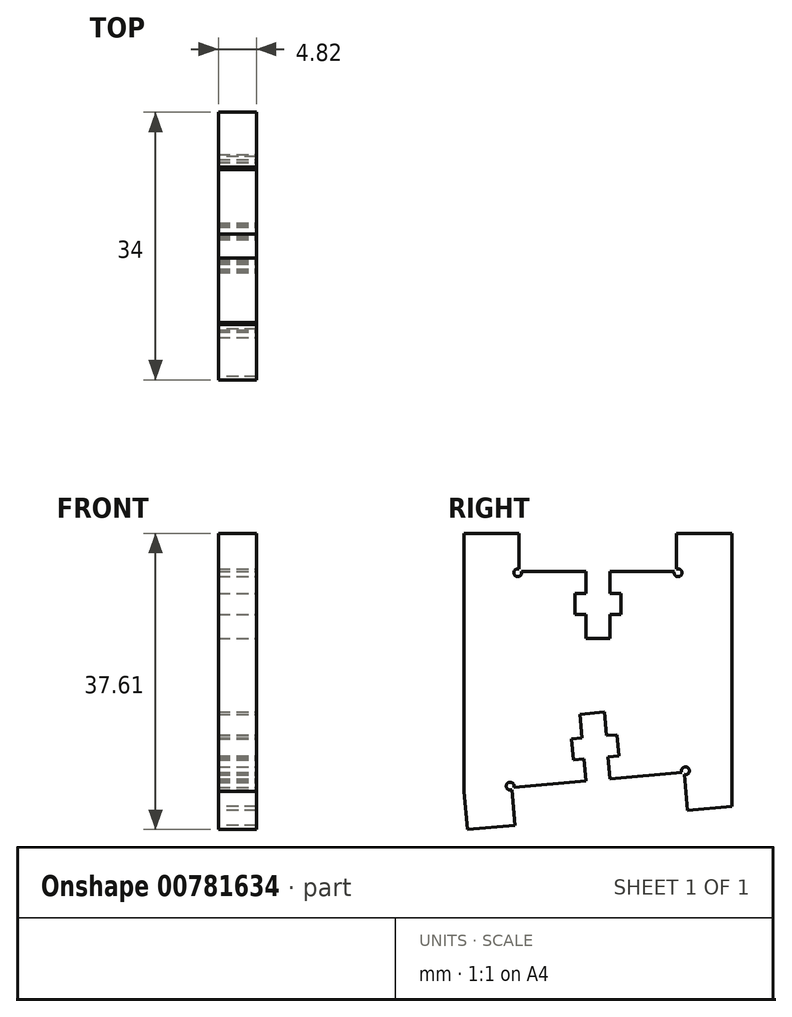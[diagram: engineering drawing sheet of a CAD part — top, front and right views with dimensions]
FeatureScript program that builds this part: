
annotation { "Feature Type Name" : "Feature", "Feature Type Description" : "" }
export const myFeature = defineFeature(function(context is Context, id is Id, definition is map)
    precondition{}
    {
        {
            var Q0;
            Q0=qCreatedBy(makeId("Right.planeOp"),FACE);
            var sketch = newSketch(context, id + "F0", { "sketchPlane" : qUnion([Q0])});
            skLineSegment(sketch, "E0.top", {"start": v(17, 0) * mm, "end": v(-17, 0) * mm});
            skLineSegment(sketch, "E0.left", {"start": v(17, -25) * mm, "end": v(17, 0) * mm});
            skLineSegment(sketch, "E0.right", {"start": v(-17, -27.97) * mm, "end": v(-17, 0) * mm});
            skPoint(sketch, "E0.middle", {"position": v(0, 0) * mm});
            skLineSegment(sketch, "E1", {"start": v(-17, -27.97) * mm, "end": v(17, -25) * mm});
            skLineSegment(sketch, "E2", {"start": v(17, -25) * mm, "end": v(-17, -25) * mm, "construction": true});
            skSolve(sketch);
        }
        {
            var Q0;
            Q0=qSketchRegion(id+"F0",true);
            extrude(context, id + "F1", {"entities" : qUnion([Q0]), "endBound" : BoundingType.SYMMETRIC, "depth" : 4.83 * mm, "offsetDistance" : 25 * mm});
        }
        {
            var Q0;
            Q0=qCreatedBy(makeId("Right.planeOp"),FACE);
            var sketch = newSketch(context, id + "F2", { "sketchPlane" : qUnion([Q0])});
            skLineSegment(sketch, "E3", {"start": v(-16.58, -32.78) * mm, "end": v(-10.54, -32.25) * mm});
            skLineSegment(sketch, "E4", {"start": v(-10.54, -32.25) * mm, "end": v(-10.96, -27.45) * mm});
            skLineSegment(sketch, "E5", {"start": v(-10.96, -27.45) * mm, "end": v(-17, -27.97) * mm});
            skLineSegment(sketch, "E6", {"start": v(-17, -27.97) * mm, "end": v(-16.58, -32.78) * mm});
            skLineSegment(sketch, "E7", {"start": v(0, -26.49) * mm, "end": v(0.68, -34.3) * mm, "construction": true});
            skLineSegment(sketch, "E8.MirrorCS", {"start": v(10.96, -25.53) * mm, "end": v(17, -25) * mm});
            skLineSegment(sketch, "E9.MirrorCS", {"start": v(11.38, -30.34) * mm, "end": v(10.96, -25.53) * mm});
            skLineSegment(sketch, "E10.MirrorCS", {"start": v(17, -29.84) * mm, "end": v(11.38, -30.34) * mm});
            skLineSegment(sketch, "E11", {"start": v(17, -25) * mm, "end": v(17, -29.84) * mm});
            skSolve(sketch);
        }
        {
            var Q0;
            Q0=qSketchRegion(id+"F2",true);
            var Q1;
            Q1=makeQuery(id+"F1.opExtrude","CAP_FACE",FACE,{"disambiguationData":[OSD([sQuery(id+"F0.wireOp",EDGE,"E0.top"),sQuery(id+"F0.wireOp",EDGE,"E0.left"),sQuery(id+"F0.wireOp",EDGE,"E0.right"),sQuery(id+"F0.wireOp",EDGE,"E1")])],"isStart":false});
            var Q2;
            Q2=makeQuery(id+"F1.opExtrude","CAP_FACE",FACE,{"disambiguationData":[OSD([sQuery(id+"F0.wireOp",EDGE,"E0.top"),sQuery(id+"F0.wireOp",EDGE,"E0.left"),sQuery(id+"F0.wireOp",EDGE,"E0.right"),sQuery(id+"F0.wireOp",EDGE,"E1")])],"isStart":true});
            extrude(context, id + "F3", {"entities" : qUnion([Q0]), "operationType" : NewBodyOperationType.ADD, "endBound" : BoundingType.UP_TO_SURFACE, "depth" : 6 * mm, "endBoundEntityFace" : qUnion([Q1]), "offsetDistance" : 25 * mm, "hasSecondDirection" : true, "secondDirectionBound" : SecondDirectionBoundingType.UP_TO_SURFACE, "secondDirectionOppositeDirection" : true, "secondDirectionDepth" : 25 * mm, "secondDirectionBoundEntityFace" : qUnion([Q2])});
        }
        {
            var Q0;
            Q0=makeQuery(id+"F3.boolean.opBoolean","MERGE",FACE,{"derivedFrom":[makeQuery(id+"F1.opExtrude","CAP_FACE",FACE,{"disambiguationData":[OSD([sQuery(id+"F0.wireOp",EDGE,"E0.top"),sQuery(id+"F0.wireOp",EDGE,"E0.left"),sQuery(id+"F0.wireOp",EDGE,"E0.right"),sQuery(id+"F0.wireOp",EDGE,"E1")])],"isStart":false}),makeQuery(id+"F3.opExtrude","CAP_FACE",FACE,{"disambiguationData":[OSD([sQuery(id+"F2.wireOp",EDGE,"E3"),sQuery(id+"F2.wireOp",EDGE,"E4"),sQuery(id+"F2.wireOp",EDGE,"E5"),sQuery(id+"F2.wireOp",EDGE,"E6")])],"isStart":false}),makeQuery(id+"F3.opExtrude","CAP_FACE",FACE,{"disambiguationData":[OSD([sQuery(id+"F2.wireOp",EDGE,"fd483ba7-293b-435a-8ddd-1c966510af4c0.MirrorCS"),sQuery(id+"F2.wireOp",EDGE,"E8.MirrorCS"),sQuery(id+"F2.wireOp",EDGE,"E9.MirrorCS"),sQuery(id+"F2.wireOp",EDGE,"E10.MirrorCS")])],"isStart":false})]});
            var sketch = newSketch(context, id + "F4", { "sketchPlane" : qUnion([Q0])});
            skLineSegment(sketch, "E12", {"start": v(-2.28, -18.15) * mm, "end": v(-2.02, -21.14) * mm});
            skLineSegment(sketch, "E13", {"start": v(-2.02, -21.14) * mm, "end": v(-3.37, -21.26) * mm});
            skLineSegment(sketch, "E14", {"start": v(-3.37, -21.26) * mm, "end": v(-3.13, -23.95) * mm});
            skLineSegment(sketch, "E15", {"start": v(-3.13, -23.95) * mm, "end": v(-1.79, -23.83) * mm});
            skLineSegment(sketch, "E16", {"start": v(-1.79, -23.83) * mm, "end": v(-1.54, -26.62) * mm});
            skLineSegment(sketch, "E17", {"start": v(-1.54, -26.62) * mm, "end": v(1.54, -26.35) * mm});
            skLineSegment(sketch, "E18", {"start": v(1.54, -26.35) * mm, "end": v(1.3, -23.56) * mm});
            skLineSegment(sketch, "E19", {"start": v(1.3, -23.56) * mm, "end": v(2.64, -23.45) * mm});
            skLineSegment(sketch, "E20", {"start": v(2.64, -23.45) * mm, "end": v(2.4, -20.76) * mm});
            skLineSegment(sketch, "E21", {"start": v(2.4, -20.76) * mm, "end": v(1.06, -20.87) * mm});
            skLineSegment(sketch, "E22", {"start": v(1.06, -20.87) * mm, "end": v(0.8, -17.88) * mm});
            skLineSegment(sketch, "E23", {"start": v(0, -26.49) * mm, "end": v(-0.74, -18.02) * mm, "construction": true});
            skLineSegment(sketch, "E24", {"start": v(-2.28, -18.15) * mm, "end": v(0.8, -17.88) * mm});
            skLineSegment(sketch, "E25", {"start": v(1.55, -8.5) * mm, "end": v(1.55, -5.5) * mm});
            skLineSegment(sketch, "E26", {"start": v(1.55, -5.5) * mm, "end": v(2.9, -5.5) * mm});
            skLineSegment(sketch, "E27", {"start": v(2.9, -5.5) * mm, "end": v(2.9, -2.8) * mm});
            skLineSegment(sketch, "E28", {"start": v(2.9, -2.8) * mm, "end": v(1.55, -2.8) * mm});
            skLineSegment(sketch, "E29", {"start": v(1.55, -2.8) * mm, "end": v(1.55, 0) * mm});
            skLineSegment(sketch, "E30", {"start": v(1.55, 0) * mm, "end": v(-1.55, 0) * mm});
            skLineSegment(sketch, "E31", {"start": v(-1.55, 0) * mm, "end": v(-1.55, -2.8) * mm});
            skLineSegment(sketch, "E32", {"start": v(-1.55, -2.8) * mm, "end": v(-2.9, -2.8) * mm});
            skLineSegment(sketch, "E33", {"start": v(-2.9, -2.8) * mm, "end": v(-2.9, -5.5) * mm});
            skLineSegment(sketch, "E34", {"start": v(-2.9, -5.5) * mm, "end": v(-1.55, -5.5) * mm});
            skLineSegment(sketch, "E35", {"start": v(-1.55, -5.5) * mm, "end": v(-1.55, -8.5) * mm});
            skLineSegment(sketch, "E36", {"start": v(0, 0) * mm, "end": v(0, -8.5) * mm, "construction": true});
            skLineSegment(sketch, "E37", {"start": v(1.55, -8.5) * mm, "end": v(-1.55, -8.5) * mm});
            skSolve(sketch);
        }
        {
            var Q0;
            Q0 = qSketchRegion(id + "F4", true);
            extrude(context, id + "F5", {"entities" : qUnion([Q0]), "operationType" : NewBodyOperationType.REMOVE, "endBound" : BoundingType.THROUGH_ALL, "oppositeDirection" : true, "depth" : 25 * mm, "offsetDistance" : 25 * mm});
        }
        {
            var Q0;
            Q0=makeQuery(id+"FRP8XEM1AVWdXp9_1.boolean.opBoolean","MERGE",FACE,{"derivedFrom":[makeQuery(id+"F3.boolean.opBoolean","MERGE",FACE,{"derivedFrom":[makeQuery(id+"F1.opExtrude","CAP_FACE",FACE,{"disambiguationData":[OSD([sQuery(id+"F0.wireOp",EDGE,"E0.top"),sQuery(id+"F0.wireOp",EDGE,"E0.left"),sQuery(id+"F0.wireOp",EDGE,"E0.right"),sQuery(id+"F0.wireOp",EDGE,"E1")])],"isStart":false}),makeQuery(id+"F3.opExtrude","CAP_FACE",FACE,{"disambiguationData":[OSD([sQuery(id+"F2.wireOp",EDGE,"E3"),sQuery(id+"F2.wireOp",EDGE,"E4"),sQuery(id+"F2.wireOp",EDGE,"E5"),sQuery(id+"F2.wireOp",EDGE,"E6")])],"isStart":false}),makeQuery(id+"F3.opExtrude","CAP_FACE",FACE,{"disambiguationData":[OSD([sQuery(id+"F2.wireOp",EDGE,"E8.MirrorCS"),sQuery(id+"F2.wireOp",EDGE,"E9.MirrorCS"),sQuery(id+"F2.wireOp",EDGE,"E10.MirrorCS"),sQuery(id+"F2.wireOp",EDGE,"E11")])],"isStart":false})]}),makeQuery(id+"FRP8XEM1AVWdXp9_1.opExtrude","CAP_FACE",FACE,{"disambiguationData":[OSD([sQuery(id+"FaWevcTfHK4qPtu_1.wireOp",EDGE,"hjG2jMZ4-9kzN-Wk7l-fv69-GlnJWHtztNU2.bottom"),sQuery(id+"FaWevcTfHK4qPtu_1.wireOp",EDGE,"hjG2jMZ4-9kzN-Wk7l-fv69-GlnJWHtztNU2.top"),sQuery(id+"FaWevcTfHK4qPtu_1.wireOp",EDGE,"hjG2jMZ4-9kzN-Wk7l-fv69-GlnJWHtztNU2.left"),sQuery(id+"FaWevcTfHK4qPtu_1.wireOp",EDGE,"hjG2jMZ4-9kzN-Wk7l-fv69-GlnJWHtztNU2.right")])],"isStart":true})]});
            var sketch = newSketch(context, id + "F6", { "sketchPlane" : qUnion([Q0])});
            skLineSegment(sketch, "E38.bottom", {"start": v(-17, 0) * mm, "end": v(-10, 0) * mm});
            skLineSegment(sketch, "E38.top", {"start": v(-17, 4.83) * mm, "end": v(-10, 4.83) * mm});
            skLineSegment(sketch, "E38.left", {"start": v(-17, 0) * mm, "end": v(-17, 4.83) * mm});
            skLineSegment(sketch, "E38.right", {"start": v(-10, 0) * mm, "end": v(-10, 4.83) * mm});
            skLineSegment(sketch, "E39.bottom", {"start": v(17, 0) * mm, "end": v(10, 0) * mm});
            skLineSegment(sketch, "E39.top", {"start": v(17, 4.83) * mm, "end": v(10, 4.83) * mm});
            skLineSegment(sketch, "E39.left", {"start": v(17, 0) * mm, "end": v(17, 4.83) * mm});
            skLineSegment(sketch, "E39.right", {"start": v(10, 0) * mm, "end": v(10, 4.83) * mm});
            skSolve(sketch);
        }
        {
            var Q0;
            Q0=makeQuery(id+"F6.imprint","IMPRINT",FACE,{"disambiguationData":[TD([[makeQuery(id+"F6.imprint","IMPRINT",EDGE,{"derivedFrom":sQuery(id+"F6.wireOp",EDGE,"E38.bottom")}),-1.0]])]});
            var Q1;
            Q1=makeQuery(id+"F6.imprint","IMPRINT",FACE,{"disambiguationData":[TD([[makeQuery(id+"F6.imprint","IMPRINT",EDGE,{"derivedFrom":sQuery(id+"F6.wireOp",EDGE,"E39.bottom")}),-1.0]])]});
            var Q2;
            {var subQ0=sQuery(id+"F2.wireOp",EDGE,"E11");var subQ1=sQuery(id+"F2.wireOp",EDGE,"E10.MirrorCS");var subQ2=sQuery(id+"F2.wireOp",EDGE,"E9.MirrorCS");var subQ3=sQuery(id+"F2.wireOp",EDGE,"E8.MirrorCS");var subQ4=sQuery(id+"F2.wireOp",EDGE,"E6");var subQ5=sQuery(id+"F2.wireOp",EDGE,"E5");var subQ6=sQuery(id+"F2.wireOp",EDGE,"E4");var subQ7=sQuery(id+"F2.wireOp",EDGE,"E3");var subQ8=sQuery(id+"F0.wireOp",EDGE,"E1");var subQ9=sQuery(id+"F0.wireOp",EDGE,"E0.right");var subQ10=sQuery(id+"F0.wireOp",EDGE,"E0.left");var subQ11=sQuery(id+"F0.wireOp",EDGE,"E0.top");Q2=makeQuery(id+"FRP8XEM1AVWdXp9_1.boolean.opBoolean","MERGE",FACE,{"derivedFrom":[makeQuery(id+"F3.boolean.opBoolean","MERGE",FACE,{"derivedFrom":[makeQuery(id+"F1.opExtrude","CAP_FACE",FACE,{"disambiguationData":[OSD([subQ11,subQ10,subQ9,subQ8])],"isStart":true}),makeQuery(id+"F3.opExtrude","CAP_FACE",FACE,{"disambiguationData":[OSD([subQ7,subQ6,subQ5,subQ4])],"isStart":true}),makeQuery(id+"F3.opExtrude","CAP_FACE",FACE,{"disambiguationData":[OSD([subQ3,subQ2,subQ1,subQ0])],"isStart":true})]}),makeQuery(id+"FRP8XEM1AVWdXp9_1.opExtrude","CAP_FACE",FACE,{"disambiguationData":[OSD([subQ11,subQ10,subQ9,subQ8,subQ7,subQ6,subQ5,subQ4,subQ3,subQ2,subQ1,subQ0])],"isStart":false})]});}
            extrude(context, id + "F7", {"entities" : qUnion([Q0, Q1]), "operationType" : NewBodyOperationType.ADD, "endBound" : BoundingType.UP_TO_SURFACE, "oppositeDirection" : true, "depth" : 25 * mm, "endBoundEntityFace" : qUnion([Q2]), "offsetDistance" : 25 * mm});
        }
        {
            var Q0;
            Q0=makeQuery(id+"FRP8XEM1AVWdXp9_1.boolean.opBoolean","MERGE",FACE,{"derivedFrom":[makeQuery(id+"F3.boolean.opBoolean","MERGE",FACE,{"derivedFrom":[makeQuery(id+"F1.opExtrude","CAP_FACE",FACE,{"disambiguationData":[OSD([sQuery(id+"F0.wireOp",EDGE,"E0.top"),sQuery(id+"F0.wireOp",EDGE,"E0.left"),sQuery(id+"F0.wireOp",EDGE,"E0.right"),sQuery(id+"F0.wireOp",EDGE,"E1")])],"isStart":false}),makeQuery(id+"F3.opExtrude","CAP_FACE",FACE,{"disambiguationData":[OSD([sQuery(id+"F2.wireOp",EDGE,"E3"),sQuery(id+"F2.wireOp",EDGE,"E4"),sQuery(id+"F2.wireOp",EDGE,"E5"),sQuery(id+"F2.wireOp",EDGE,"E6")])],"isStart":false}),makeQuery(id+"F3.opExtrude","CAP_FACE",FACE,{"disambiguationData":[OSD([sQuery(id+"F2.wireOp",EDGE,"E8.MirrorCS"),sQuery(id+"F2.wireOp",EDGE,"E9.MirrorCS"),sQuery(id+"F2.wireOp",EDGE,"E10.MirrorCS"),sQuery(id+"F2.wireOp",EDGE,"E11")])],"isStart":false})]}),makeQuery(id+"FRP8XEM1AVWdXp9_1.opExtrude","CAP_FACE",FACE,{"disambiguationData":[OSD([sQuery(id+"FaWevcTfHK4qPtu_1.wireOp",EDGE,"hjG2jMZ4-9kzN-Wk7l-fv69-GlnJWHtztNU2.bottom"),sQuery(id+"FaWevcTfHK4qPtu_1.wireOp",EDGE,"hjG2jMZ4-9kzN-Wk7l-fv69-GlnJWHtztNU2.top"),sQuery(id+"FaWevcTfHK4qPtu_1.wireOp",EDGE,"hjG2jMZ4-9kzN-Wk7l-fv69-GlnJWHtztNU2.left"),sQuery(id+"FaWevcTfHK4qPtu_1.wireOp",EDGE,"hjG2jMZ4-9kzN-Wk7l-fv69-GlnJWHtztNU2.right")])],"isStart":true})]});
            var sketch = newSketch(context, id + "F8", { "sketchPlane" : qUnion([Q0])});
            skLineSegment(sketch, "E40", {"start": v(10.96, -25.53) * mm, "end": v(11.12, -25.34) * mm, "construction": true});
            skLineSegment(sketch, "E41", {"start": v(-10.96, -27.45) * mm, "end": v(-11.15, -27.29) * mm, "construction": true});
            skCircle(sketch, "E42", {"center": v(-11.15, -27.29) * mm, "radius": 0.5 * mm});
            skCircle(sketch, "E43", {"center": v(11.12, -25.34) * mm, "radius": 0.5 * mm});
            skLineSegment(sketch, "E44", {"start": v(-10, 0) * mm, "end": v(-10.18, -0.18) * mm, "construction": true});
            skCircle(sketch, "E45", {"center": v(-10.18, -0.18) * mm, "radius": 0.5 * mm});
            skLineSegment(sketch, "E46", {"start": v(0, 0) * mm, "end": v(0, -8.5) * mm, "construction": true});
            skLineSegment(sketch, "E47.MirrorCS", {"start": v(10, 0) * mm, "end": v(10.18, -0.18) * mm, "construction": true});
            skCircle(sketch, "E48.MirrorC", {"center": v(10.18, -0.18) * mm, "radius": 0.5 * mm});
            skSolve(sketch);
        }
        {
            var Q0;
            Q0 = qSketchRegion(id + "F8", true);
            extrude(context, id + "F9", {"entities" : qUnion([Q0]), "operationType" : NewBodyOperationType.REMOVE, "endBound" : BoundingType.THROUGH_ALL, "oppositeDirection" : true, "depth" : 25 * mm, "offsetDistance" : 25 * mm});
        }
    });
